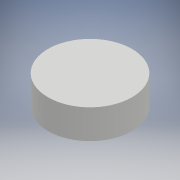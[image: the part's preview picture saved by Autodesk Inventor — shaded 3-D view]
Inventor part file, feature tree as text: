
AUTODESK INVENTOR PART (.ipt)
format: ipt  version: 2018 (Build 220112000, 112)  size: 121,344 bytes
history: native  units: mm
features: other x3, extrude x3, sketch x3
ambient origin geometry x8: Origin, YZ Plane, XZ Plane, XY Plane, X Axis, Y Axis, Z Axis, Center Point
bodies: Solide1 (feature_tree)
feature tree (9):
  other  "Annotations"
  extrude  "Extrusion1"  Depth=41.0mm
  extrude  "Extrusion2"  Depth=43.0mm
  extrude  "Extrusion3"  Depth=15.0mm TaperAngle=0.0deg
  sketch  "Esquisse1"
  sketch  "Esquisse2"
  sketch  "Esquisse3"
  other  "Cote linéaire 1"
  other  "Cote linéaire 2"
